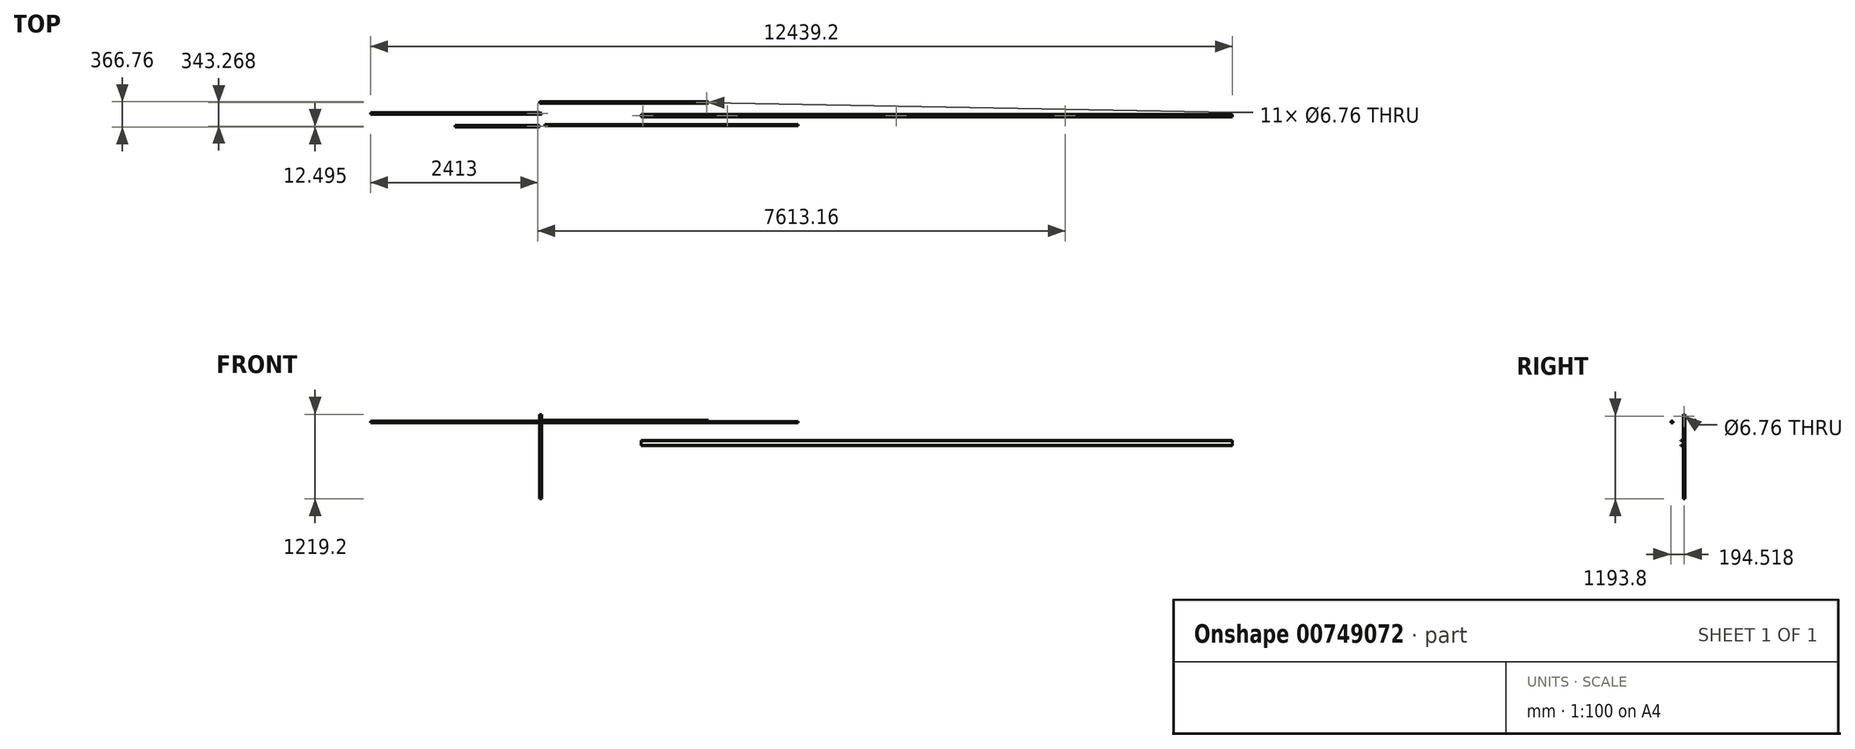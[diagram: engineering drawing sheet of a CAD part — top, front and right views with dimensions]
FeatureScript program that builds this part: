
annotation { "Feature Type Name" : "Feature", "Feature Type Description" : "" }
export const myFeature = defineFeature(function(context is Context, id is Id, definition is map)
    precondition{}
    {
        {
            var Q0;
            Q0=qCreatedBy(makeId("Top.planeOp"),FACE);
            var sketch = newSketch(context, id + "F0", { "sketchPlane" : qUnion([Q0])});
            skLineSegment(sketch, "E0.bottom", {"start": v(0, 0) * mm, "end": v(-2438.4, 0) * mm});
            skLineSegment(sketch, "E0.top", {"start": v(0, 25) * mm, "end": v(-2438.4, 25) * mm});
            skLineSegment(sketch, "E0.left", {"start": v(0, 0) * mm, "end": v(0, 25) * mm});
            skLineSegment(sketch, "E0.right", {"start": v(-2438.4, 0) * mm, "end": v(-2438.4, 25) * mm});
            skPoint(sketch, "E1", {"position": v(-25.4, 12.5) * mm});
            skPoint(sketch, "E1.positionSnap0", {"position": v(0, 12.5) * mm});
            skSolve(sketch);
        }
        {
            var Q0;
            Q0 = qSketchRegion(id + "F0", true);
            extrude(context, id + "F1", {"entities" : qUnion([Q0]), "depth" : 24.75 * mm, "offsetDistance" : 25 * mm});
        }
        {
            var Q0;
            Q0=qCreatedBy(makeId("Top.planeOp"),FACE);
            var sketch = newSketch(context, id + "F2", { "sketchPlane" : qUnion([Q0])});
            skLineSegment(sketch, "E2.bottom", {"start": v(76.2, -147.98) * mm, "end": v(3733.8, -147.98) * mm});
            skLineSegment(sketch, "E2.top", {"start": v(76.2, -167.03) * mm, "end": v(3733.8, -167.03) * mm});
            skLineSegment(sketch, "E2.left", {"start": v(76.2, -147.98) * mm, "end": v(76.2, -167.03) * mm});
            skLineSegment(sketch, "E2.right", {"start": v(3733.8, -147.98) * mm, "end": v(3733.8, -167.03) * mm});
            skSolve(sketch);
        }
        {
            var Q0;
            Q0 = qSketchRegion(id + "F2", true);
            extrude(context, id + "F3", {"entities" : qUnion([Q0]), "depth" : 15.88 * mm, "offsetDistance" : 25.4 * mm});
        }
        {
            var Q0;
            Q0=qCreatedBy(makeId("Top.planeOp"),FACE);
            var sketch = newSketch(context, id + "F4", { "sketchPlane" : qUnion([Q0])});
            skLineSegment(sketch, "E3.bottom", {"start": v(0, 183.24) * mm, "end": v(2438.4, 183.24) * mm});
            skLineSegment(sketch, "E3.top", {"start": v(0, 161.24) * mm, "end": v(2438.4, 161.24) * mm});
            skLineSegment(sketch, "E3.left", {"start": v(0, 183.24) * mm, "end": v(0, 161.24) * mm});
            skLineSegment(sketch, "E3.right", {"start": v(2438.4, 183.24) * mm, "end": v(2438.4, 161.24) * mm});
            skPoint(sketch, "E4", {"position": v(2413, 172.24) * mm});
            skPoint(sketch, "E4.positionSnap0", {"position": v(2438.4, 172.24) * mm});
            skSolve(sketch);
        }
        {
            var Q0;
            Q0 = qSketchRegion(id + "F4", true);
            extrude(context, id + "F5", {"entities" : qUnion([Q0]), "depth" : 33.53 * mm, "offsetDistance" : 25.4 * mm});
        }
        {
            var Q0;
            Q0=qCreatedBy(makeId("Right.planeOp"),FACE);
            var sketch = newSketch(context, id + "F6", { "sketchPlane" : qUnion([Q0])});
            skLineSegment(sketch, "E5.bottom", {"start": v(0, 120.8) * mm, "end": v(22, 120.8) * mm});
            skLineSegment(sketch, "E5.top", {"start": v(0, -1098.4) * mm, "end": v(22, -1098.4) * mm});
            skLineSegment(sketch, "E5.left", {"start": v(0, 120.8) * mm, "end": v(0, -1098.4) * mm});
            skLineSegment(sketch, "E5.right", {"start": v(22, 120.8) * mm, "end": v(22, -1098.4) * mm});
            skPoint(sketch, "E6", {"position": v(11, 95.4) * mm});
            skPoint(sketch, "E6.positionSnap0", {"position": v(11, 120.8) * mm});
            skSolve(sketch);
        }
        {
            var Q0;
            Q0 = qSketchRegion(id + "F6", true);
            extrude(context, id + "F7", {"entities" : qUnion([Q0]), "depth" : 33.53 * mm, "offsetDistance" : 25.4 * mm});
        }
        {
            var Q0;
            Q0=qCreatedBy(makeId("Front.planeOp"),FACE);
            var sketch = newSketch(context, id + "F8", { "sketchPlane" : qUnion([Q0])});
            skLineSegment(sketch, "E7.bottom", {"start": v(1466.36, -332.16) * mm, "end": v(10000.76, -332.16) * mm});
            skLineSegment(sketch, "E7.top", {"start": v(1466.36, -255.96) * mm, "end": v(10000.76, -255.96) * mm});
            skLineSegment(sketch, "E7.left", {"start": v(1466.36, -332.16) * mm, "end": v(1466.36, -255.96) * mm});
            skLineSegment(sketch, "E7.right", {"start": v(10000.76, -332.16) * mm, "end": v(10000.76, -255.96) * mm});
            skSolve(sketch);
        }
        {
            var Q0;
            Q0 = qSketchRegion(id + "F8", true);
            extrude(context, id + "F9", {"entities" : qUnion([Q0]), "depth" : 38.1 * mm, "offsetDistance" : 25.4 * mm});
        }
        {
            var Q0;
            Q0=makeQuery(id+"F9.opExtrude","SWEPT_FACE",FACE,{"disambiguationData":[OSD([sQuery(id+"F8.wireOp",EDGE,"E7.right")])]});
            var sketch = newSketch(context, id + "F10", { "sketchPlane" : qUnion([Q0])});
            skLineSegment(sketch, "E8", {"start": v(0, -294.06) * mm, "end": v(-38.1, -294.06) * mm, "construction": true});
            skLineSegment(sketch, "E9.bottom", {"start": v(-4.32, -327.84) * mm, "end": v(-71.88, -327.84) * mm});
            skLineSegment(sketch, "E9.top", {"start": v(-4.32, -260.28) * mm, "end": v(-71.88, -260.28) * mm});
            skLineSegment(sketch, "E9.left", {"start": v(-4.32, -327.84) * mm, "end": v(-4.32, -260.28) * mm});
            skLineSegment(sketch, "E9.right", {"start": v(-71.88, -327.84) * mm, "end": v(-71.88, -260.28) * mm});
            skPoint(sketch, "E9.middle", {"position": v(-38.1, -294.06) * mm});
            skSolve(sketch);
        }
        {
            var Q0;
            Q0 = qSketchRegion(id + "F10", true);
            extrude(context, id + "F11", {"entities" : qUnion([Q0]), "operationType" : NewBodyOperationType.REMOVE, "oppositeDirection" : true, "depth" : 8534.4 * mm, "offsetDistance" : 25.4 * mm});
        }
        {
            var Q0;
            Q0=makeQuery(id+"F9.opExtrude","SWEPT_FACE",FACE,{"disambiguationData":[OSD([sQuery(id+"F8.wireOp",EDGE,"E7.top")])]});
            var sketch = newSketch(context, id + "F12", { "sketchPlane" : qUnion([Q0])});
            skPoint(sketch, "E10", {"position": v(1491.76, -19.05) * mm});
            skPoint(sketch, "E10.positionSnap0", {"position": v(1466.36, -19.05) * mm});
            skPoint(sketch, "E11", {"position": v(2710.96, -19.05) * mm});
            skPoint(sketch, "E12", {"position": v(5149.36, -19.05) * mm});
            skPoint(sketch, "E13", {"position": v(7587.76, -19.05) * mm});
            skSolve(sketch);
        }
        {
            var Q0;
            Q0=makeQuery(id+"F9.opExtrude","SWEPT_FACE",FACE,{"disambiguationData":[OSD([sQuery(id+"F8.wireOp",EDGE,"E7.bottom")])]});
            var sketch = newSketch(context, id + "F13", { "sketchPlane" : qUnion([Q0])});
            skPoint(sketch, "E14", {"position": v(1491.76, 19.05) * mm});
            skPoint(sketch, "E14.positionSnap0", {"position": v(1466.36, 19.05) * mm});
            skPoint(sketch, "E15", {"position": v(2710.96, 19.05) * mm});
            skPoint(sketch, "E16", {"position": v(5149.36, 19.05) * mm});
            skPoint(sketch, "E17", {"position": v(7587.76, 19.05) * mm});
            skSolve(sketch);
        }
        {
            var Q0;
            Q0=sQuery(id+"F13.wireOp",VERTEX,"E14");
            var Q1;
            Q1=sQuery(id+"F12.wireOp",VERTEX,"E10");
            var Q2;
            Q2=makeQuery(id+"F9.opExtrude","SWEPT_BODY",BODY,{"disambiguationData":[OSD([sQuery(id+"F8.wireOp",EDGE,"E7.bottom"),sQuery(id+"F8.wireOp",EDGE,"E7.top"),sQuery(id+"F8.wireOp",EDGE,"E7.left"),sQuery(id+"F8.wireOp",EDGE,"E7.right")])]});
            hole(context, id + "F14", {"style" : HoleStyle.SIMPLE, "endStyle" : HoleEndStyle.BLIND, "standardTappedOrClearance" : lookupTablePath({ "standard" : "ANSI", "fit" : "Normal (ASME)", "size" : "1/4", "type" : "Clearance" }), "standardBlindInLast" : lookupTablePath({ "fit" : "Free", "standard" : "ANSI", "size" : "1/4", "type" : "Clearance" }), "holeDiameter" : 6.76 * mm, "majorDiameter" : 6.35 * mm, "holeDepth" : 19.68 * mm, "isTappedThrough" : true, "tappedDepth" : 15.88 * mm, "tapClearance" : 3, "locations" : qUnion([Q0, Q1]), "scope" : qUnion([Q2])});
        }
        {
            var Q0;
            Q0=sQuery(id+"F13.wireOp",VERTEX,"E15");
            var Q1;
            Q1=sQuery(id+"F13.wireOp",VERTEX,"E16");
            var Q2;
            Q2=sQuery(id+"F13.wireOp",VERTEX,"E17");
            var Q3;
            Q3=makeQuery(id+"F9.opExtrude","SWEPT_BODY",BODY,{"disambiguationData":[OSD([sQuery(id+"F8.wireOp",EDGE,"E7.bottom"),sQuery(id+"F8.wireOp",EDGE,"E7.top"),sQuery(id+"F8.wireOp",EDGE,"E7.left"),sQuery(id+"F8.wireOp",EDGE,"E7.right")])]});
            hole(context, id + "F15", {"style" : HoleStyle.SIMPLE, "endStyle" : HoleEndStyle.BLIND, "standardTappedOrClearance" : lookupTablePath({ "standard" : "ANSI", "fit" : "Normal (ASME)", "size" : "1/4", "type" : "Clearance" }), "standardBlindInLast" : lookupTablePath({ "fit" : "Free", "standard" : "ANSI", "size" : "1/4", "type" : "Clearance" }), "holeDiameter" : 6.76 * mm, "majorDiameter" : 6.35 * mm, "holeDepth" : 19.68 * mm, "isTappedThrough" : true, "tappedDepth" : 15.88 * mm, "tapClearance" : 3, "locations" : qUnion([Q0, Q1, Q2]), "scope" : qUnion([Q3])});
        }
        {
            var Q0;
            Q0=sQuery(id+"F12.wireOp",VERTEX,"E10");
            var Q1;
            Q1=sQuery(id+"F12.wireOp",VERTEX,"E11");
            var Q2;
            Q2=sQuery(id+"F12.wireOp",VERTEX,"E12");
            var Q3;
            Q3=sQuery(id+"F12.wireOp",VERTEX,"E13");
            var Q4;
            Q4=makeQuery(id+"F9.opExtrude","SWEPT_BODY",BODY,{"disambiguationData":[OSD([sQuery(id+"F8.wireOp",EDGE,"E7.bottom"),sQuery(id+"F8.wireOp",EDGE,"E7.top"),sQuery(id+"F8.wireOp",EDGE,"E7.left"),sQuery(id+"F8.wireOp",EDGE,"E7.right")])]});
            hole(context, id + "F16", {"style" : HoleStyle.SIMPLE, "endStyle" : HoleEndStyle.BLIND, "standardTappedOrClearance" : lookupTablePath({ "standard" : "ANSI", "fit" : "Normal (ASME)", "size" : "1/4", "type" : "Clearance" }), "standardBlindInLast" : lookupTablePath({ "fit" : "Free", "standard" : "ANSI", "size" : "1/4", "type" : "Clearance" }), "holeDiameter" : 6.76 * mm, "majorDiameter" : 6.35 * mm, "holeDepth" : 19.68 * mm, "isTappedThrough" : true, "tappedDepth" : 15.88 * mm, "tapClearance" : 3, "locations" : qUnion([Q0, Q1, Q2, Q3]), "scope" : qUnion([Q4])});
        }
        {
            var Q0;
            Q0=qCreatedBy(makeId("Top.planeOp"),FACE);
            var sketch = newSketch(context, id + "F17", { "sketchPlane" : qUnion([Q0])});
            skLineSegment(sketch, "E18.bottom", {"start": v(0, -158.53) * mm, "end": v(-1219.2, -158.53) * mm});
            skLineSegment(sketch, "E18.top", {"start": v(0, -183.52) * mm, "end": v(-1219.2, -183.52) * mm});
            skLineSegment(sketch, "E18.left", {"start": v(0, -158.53) * mm, "end": v(0, -183.52) * mm});
            skLineSegment(sketch, "E18.right", {"start": v(-1219.2, -158.53) * mm, "end": v(-1219.2, -183.52) * mm});
            skPoint(sketch, "E19", {"position": v(-25.4, -171.02) * mm});
            skPoint(sketch, "E19.positionSnap0", {"position": v(0, -171.02) * mm});
            skSolve(sketch);
        }
        {
            var Q0;
            Q0 = qSketchRegion(id + "F17", true);
            extrude(context, id + "F18", {"entities" : qUnion([Q0]), "depth" : 24.74 * mm, "offsetDistance" : 25.4 * mm});
        }
        {
            var Q0;
            Q0=sQuery(id+"F17.wireOp",VERTEX,"E19");
            var Q1;
            Q1=makeQuery(id+"F18.opExtrude","SWEPT_BODY",BODY,{"disambiguationData":[OSD([sQuery(id+"F17.wireOp",EDGE,"E18.bottom"),sQuery(id+"F17.wireOp",EDGE,"E18.top"),sQuery(id+"F17.wireOp",EDGE,"E18.left"),sQuery(id+"F17.wireOp",EDGE,"E18.right")])]});
            hole(context, id + "F19", {"style" : HoleStyle.SIMPLE, "endStyle" : HoleEndStyle.BLIND, "oppositeDirection" : true, "standardTappedOrClearance" : lookupTablePath({ "standard" : "ANSI", "fit" : "Normal (ASME)", "size" : "1/4", "type" : "Clearance" }), "standardBlindInLast" : lookupTablePath({ "fit" : "Free", "standard" : "ANSI", "size" : "1/4", "type" : "Clearance" }), "holeDiameter" : 6.76 * mm, "majorDiameter" : 6.35 * mm, "holeDepth" : 19.68 * mm, "isTappedThrough" : true, "tappedDepth" : 15.88 * mm, "tapClearance" : 3, "locations" : qUnion([Q0]), "scope" : qUnion([Q1])});
        }
        {
            var Q0;
            Q0=sQuery(id+"F0.wireOp",VERTEX,"E1");
            var Q1;
            Q1=makeQuery(id+"F1.opExtrude","SWEPT_BODY",BODY,{"disambiguationData":[OSD([sQuery(id+"F0.wireOp",EDGE,"E0.bottom"),sQuery(id+"F0.wireOp",EDGE,"E0.top"),sQuery(id+"F0.wireOp",EDGE,"E0.left"),sQuery(id+"F0.wireOp",EDGE,"E0.right")])]});
            hole(context, id + "F20", {"style" : HoleStyle.SIMPLE, "endStyle" : HoleEndStyle.BLIND, "oppositeDirection" : true, "standardTappedOrClearance" : lookupTablePath({ "standard" : "ANSI", "fit" : "Normal (ASME)", "size" : "1/4", "type" : "Clearance" }), "standardBlindInLast" : lookupTablePath({ "fit" : "Free", "standard" : "ANSI", "size" : "1/4", "type" : "Clearance" }), "holeDiameter" : 6.76 * mm, "majorDiameter" : 6.35 * mm, "holeDepth" : 19.68 * mm, "isTappedThrough" : true, "tappedDepth" : 15.88 * mm, "tapClearance" : 3, "locations" : qUnion([Q0]), "scope" : qUnion([Q1])});
        }
        {
            var Q0;
            Q0=sQuery(id+"F4.wireOp",VERTEX,"E4");
            var Q1;
            Q1=makeQuery(id+"F5.opExtrude","SWEPT_BODY",BODY,{"disambiguationData":[OSD([sQuery(id+"F4.wireOp",EDGE,"E3.bottom"),sQuery(id+"F4.wireOp",EDGE,"E3.top"),sQuery(id+"F4.wireOp",EDGE,"E3.left"),sQuery(id+"F4.wireOp",EDGE,"E3.right")])]});
            hole(context, id + "F21", {"style" : HoleStyle.SIMPLE, "endStyle" : HoleEndStyle.BLIND, "oppositeDirection" : true, "standardTappedOrClearance" : lookupTablePath({ "standard" : "ANSI", "fit" : "Normal (ASME)", "size" : "1/4", "type" : "Clearance" }), "standardBlindInLast" : lookupTablePath({ "fit" : "Free", "standard" : "ANSI", "size" : "1/4", "type" : "Clearance" }), "holeDiameter" : 6.76 * mm, "majorDiameter" : 6.35 * mm, "holeDepth" : 19.68 * mm, "isTappedThrough" : true, "tappedDepth" : 15.88 * mm, "tapClearance" : 3, "locations" : qUnion([Q0]), "scope" : qUnion([Q1])});
        }
        {
            var Q0;
            Q0=sQuery(id+"F6.wireOp",VERTEX,"E6");
            var Q1;
            Q1=makeQuery(id+"F7.opExtrude","SWEPT_BODY",BODY,{"disambiguationData":[OSD([sQuery(id+"F6.wireOp",EDGE,"E5.bottom"),sQuery(id+"F6.wireOp",EDGE,"E5.top"),sQuery(id+"F6.wireOp",EDGE,"E5.left"),sQuery(id+"F6.wireOp",EDGE,"E5.right")])]});
            hole(context, id + "F22", {"style" : HoleStyle.SIMPLE, "endStyle" : HoleEndStyle.BLIND, "oppositeDirection" : true, "standardTappedOrClearance" : lookupTablePath({ "standard" : "ANSI", "fit" : "Normal (ASME)", "size" : "1/4", "type" : "Clearance" }), "standardBlindInLast" : lookupTablePath({ "fit" : "Free", "standard" : "ANSI", "size" : "1/4", "type" : "Clearance" }), "holeDiameter" : 6.76 * mm, "majorDiameter" : 6.35 * mm, "holeDepth" : 19.68 * mm, "isTappedThrough" : true, "tappedDepth" : 15.88 * mm, "tapClearance" : 3, "locations" : qUnion([Q0]), "scope" : qUnion([Q1])});
        }
    });
